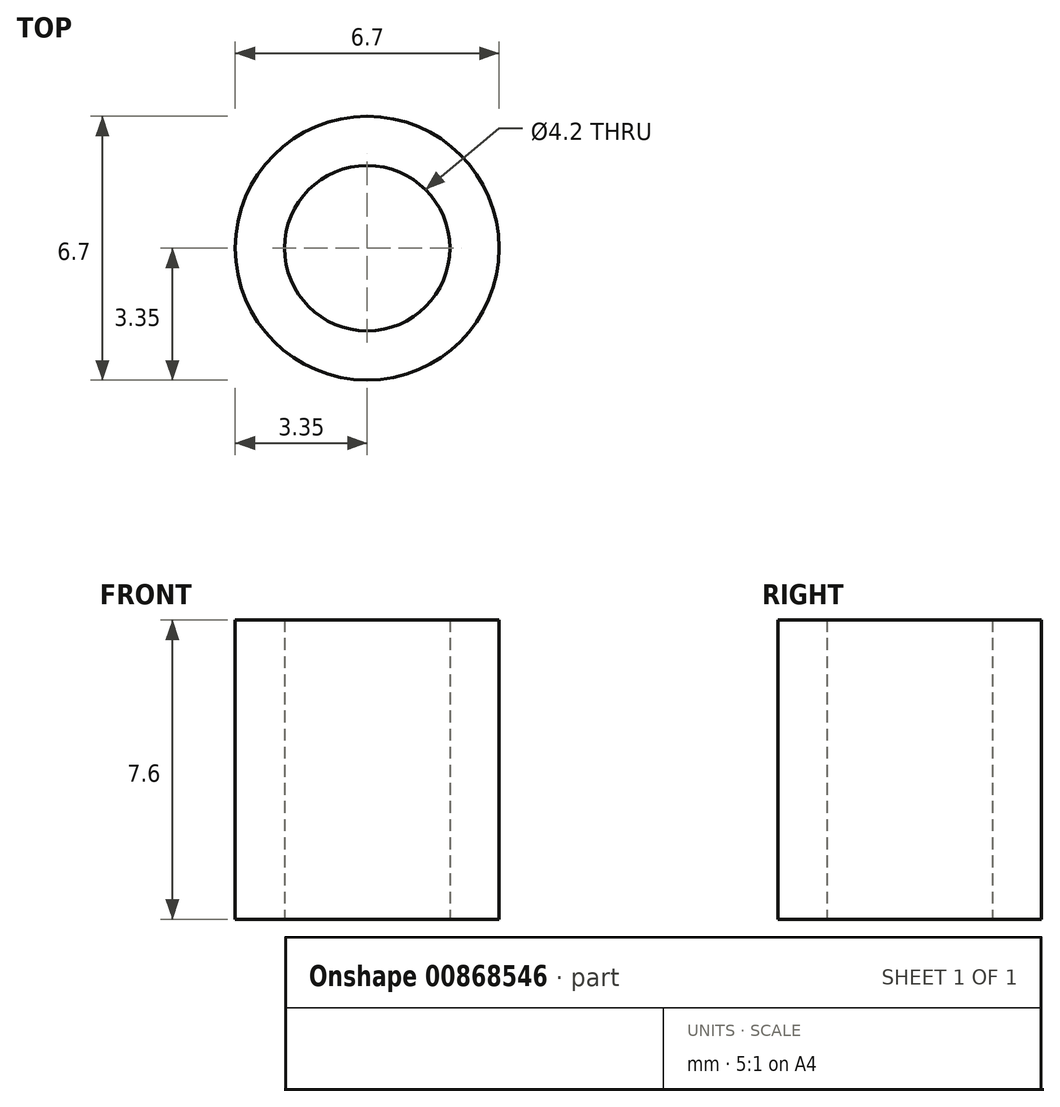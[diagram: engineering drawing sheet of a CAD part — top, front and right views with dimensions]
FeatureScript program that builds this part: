
annotation { "Feature Type Name" : "Feature", "Feature Type Description" : "" }
export const myFeature = defineFeature(function(context is Context, id is Id, definition is map)
    precondition{}
    {
        {
            var Q0;
            Q0=qCreatedBy(makeId("Top.planeOp"),FACE);
            var sketch = newSketch(context, id + "F0", { "sketchPlane" : qUnion([Q0])});
            skCircle(sketch, "E0", {"center": v(0, 0) * mm, "radius": 2.1 * mm});
            skCircle(sketch, "E1", {"center": v(0, 0) * mm, "radius": 3.35 * mm});
            skSolve(sketch);
        }
        {
            var Q0;
            Q0 = qSketchRegion(id + "F0", true);
            extrude(context, id + "F1", {"entities" : qUnion([Q0]), "depth" : 7.6 * mm, "offsetDistance" : 25 * mm});
        }
    });
